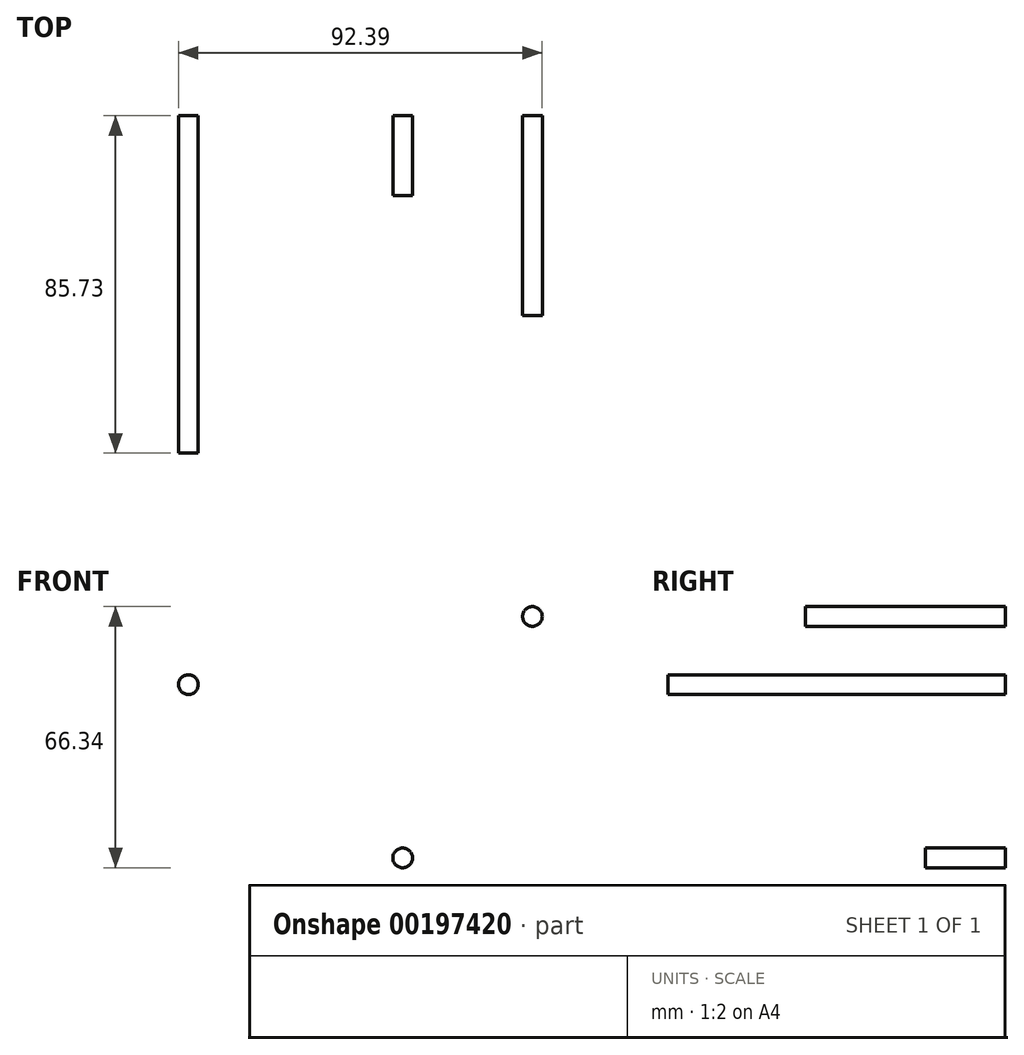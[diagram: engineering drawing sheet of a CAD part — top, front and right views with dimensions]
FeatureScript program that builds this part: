
annotation { "Feature Type Name" : "Feature", "Feature Type Description" : "" }
export const myFeature = defineFeature(function(context is Context, id is Id, definition is map)
    precondition{}
    {
        {
            var Q0;
            Q0=qCreatedBy(makeId("Front.planeOp"),FACE);
            var sketch = newSketch(context, id + "F0", { "sketchPlane" : qUnion([Q0])});
            skCircle(sketch, "E0", {"center": v(0, 0) * mm, "radius": 2.5 * mm});
            skSolve(sketch);
        }
        {
            var Q0;
            Q0 = qSketchRegion(id + "F0", true);
            extrude(context, id + "F1", {"entities" : qUnion([Q0]), "depth" : 20.32 * mm});
        }
        {
            var Q0;
            Q0=qCreatedBy(makeId("Front.planeOp"),FACE);
            var sketch = newSketch(context, id + "F2", { "sketchPlane" : qUnion([Q0])});
            skCircle(sketch, "E1", {"center": v(-54.43, 44.03) * mm, "radius": 2.5 * mm});
            skSolve(sketch);
        }
        {
            var Q0;
            Q0 = qSketchRegion(id + "F2", true);
            extrude(context, id + "F3", {"entities" : qUnion([Q0]), "depth" : 85.72 * mm});
        }
        {
            var Q0;
            Q0=qCreatedBy(makeId("Front.planeOp"),FACE);
            var sketch = newSketch(context, id + "F4", { "sketchPlane" : qUnion([Q0])});
            skCircle(sketch, "E2", {"center": v(32.96, 61.34) * mm, "radius": 2.5 * mm});
            skSolve(sketch);
        }
        {
            var Q0;
            Q0 = qSketchRegion(id + "F4", true);
            extrude(context, id + "F5", {"entities" : qUnion([Q0]), "depth" : 50.8 * mm});
        }
    });
